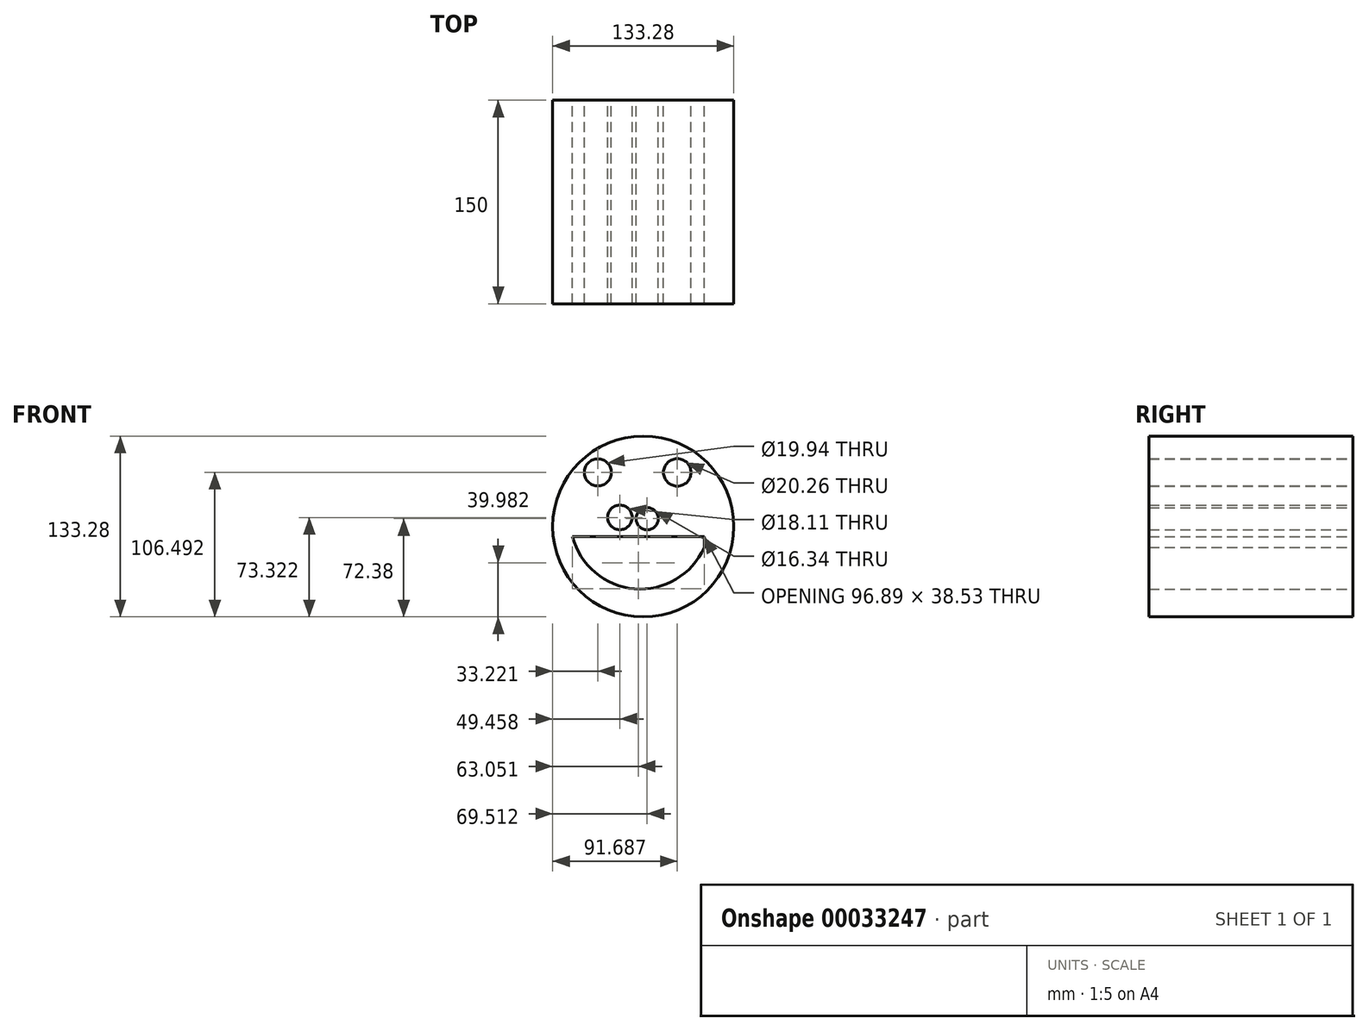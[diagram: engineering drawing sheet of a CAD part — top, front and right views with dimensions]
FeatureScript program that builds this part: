
annotation { "Feature Type Name" : "Feature", "Feature Type Description" : "" }
export const myFeature = defineFeature(function(context is Context, id is Id, definition is map)
    precondition{}
    {
        {
            var Q0;
            Q0=qCreatedBy(makeId("Front.planeOp"),FACE);
            var sketch = newSketch(context, id + "F0", { "sketchPlane" : qUnion([Q0])});
            skCircle(sketch, "E0", {"center": v(0, 0) * mm, "radius": 66.64 * mm});
            skCircle(sketch, "E1", {"center": v(-33.42, 39.85) * mm, "radius": 9.97 * mm});
            skCircle(sketch, "E2", {"center": v(25.05, 39.85) * mm, "radius": 10.13 * mm});
            skArc(sketch, "E3", {"start": v(-52.03, -7.4) * mm, "mid": v(-6.48, -45.92) * mm, "end": v(44.85, -15.52) * mm});
            skLineSegment(sketch, "E4", {"start": v(-52.03, -7.4) * mm, "end": v(44.85, -7.4) * mm});
            skLineSegment(sketch, "E5", {"start": v(44.85, -7.4) * mm, "end": v(44.85, -15.52) * mm});
            skLineSegment(sketch, "E6", {"start": v(-47.21, -19.54) * mm, "end": v(42.85, -19.54) * mm});
            skLineSegment(sketch, "E7", {"start": v(-34.14, -7.4) * mm, "end": v(-34.14, -34.98) * mm});
            skLineSegment(sketch, "E8", {"start": v(-21.01, -7.4) * mm, "end": v(-21.01, -42.53) * mm});
            skLineSegment(sketch, "E9", {"start": v(-8.13, -7.4) * mm, "end": v(-8.13, -45.76) * mm});
            skLineSegment(sketch, "E10", {"start": v(5.24, -7.4) * mm, "end": v(5.24, -45.56) * mm});
            skLineSegment(sketch, "E11", {"start": v(14.78, -7.4) * mm, "end": v(14.78, -43.23) * mm});
            skLineSegment(sketch, "E12", {"start": v(23.91, -39) * mm, "end": v(23.91, -7.4) * mm});
            skLineSegment(sketch, "E13", {"start": v(32.68, -7.4) * mm, "end": v(32.68, -32.5) * mm});
            skCircle(sketch, "E14", {"center": v(-17.18, 6.68) * mm, "radius": 9.06 * mm});
            skCircle(sketch, "E15", {"center": v(2.87, 5.74) * mm, "radius": 8.17 * mm});
            skLineSegment(sketch, "E16", {"start": v(-11.23, 13.5) * mm, "end": v(-11.23, 25.53) * mm});
            skLineSegment(sketch, "E17", {"start": v(-11.23, 25.53) * mm, "end": v(-7.79, 23.13) * mm});
            skSolve(sketch);
        }
        {
            var Q0;
            Q0=makeQuery(id+"F0.imprint","IMPRINT",FACE,{"disambiguationData":[TD([[makeQuery(id+"F0.imprint","IMPRINT",EDGE,{"derivedFrom":sQuery(id+"F0.wireOp",EDGE,"E0")}),1.0]])]});
            extrude(context, id + "F1", {"entities" : qUnion([Q0]), "depth" : 150 * mm});
        }
    });
